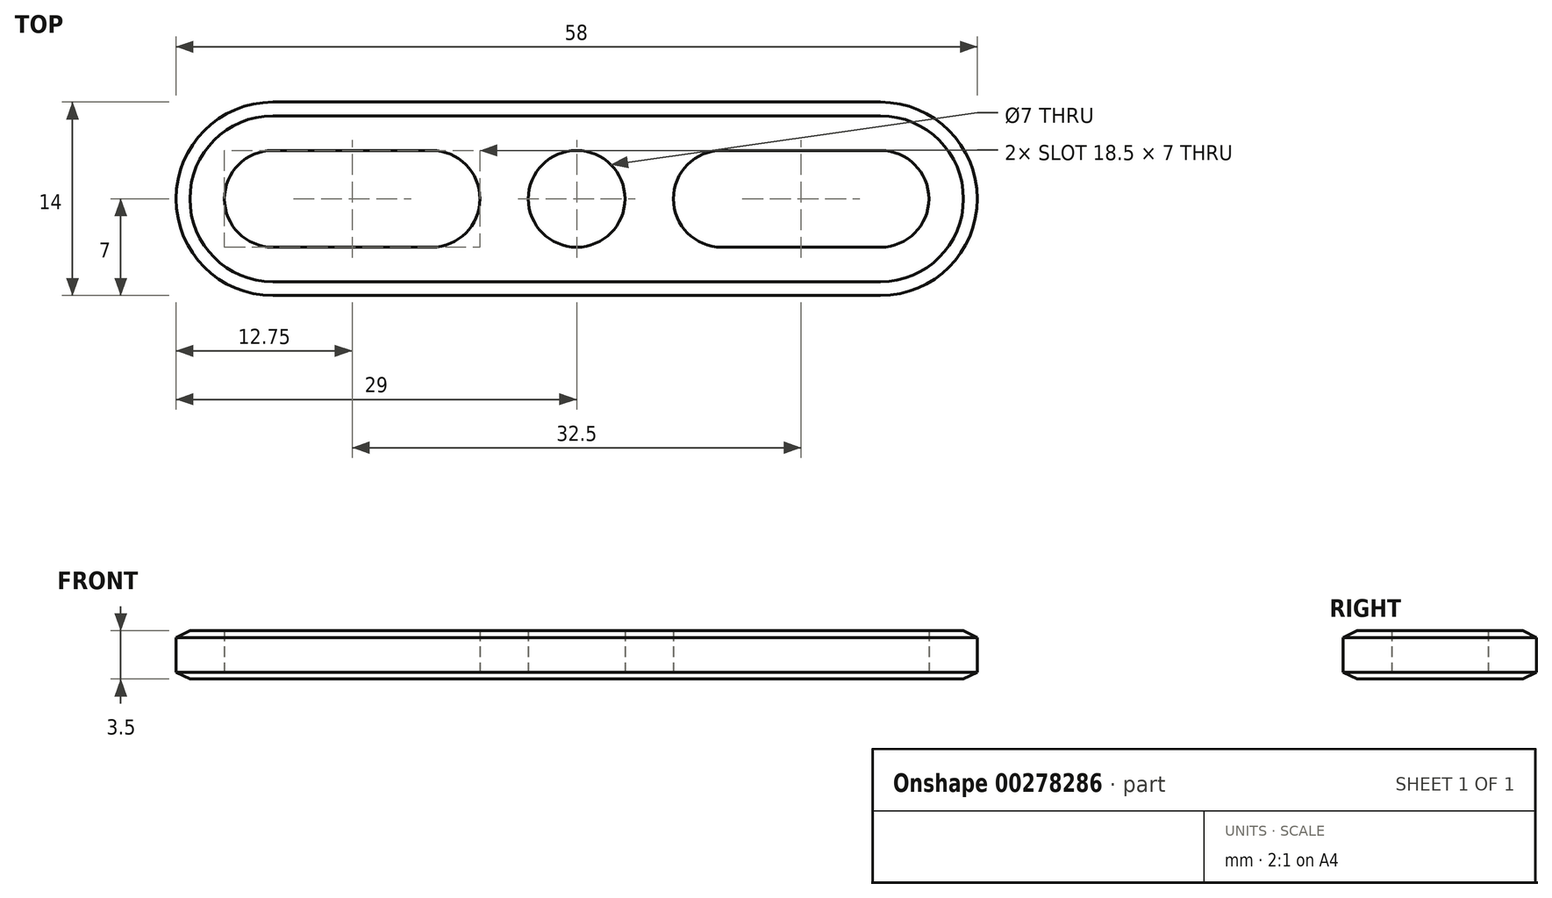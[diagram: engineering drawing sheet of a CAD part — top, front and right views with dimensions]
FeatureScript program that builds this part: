
annotation { "Feature Type Name" : "Feature", "Feature Type Description" : "" }
export const myFeature = defineFeature(function(context is Context, id is Id, definition is map)
    precondition{}
    {
        {
            var Q0;
            Q0=qCreatedBy(makeId("Top.planeOp"),FACE);
            var sketch = newSketch(context, id + "F0", { "sketchPlane" : qUnion([Q0])});
            skLineSegment(sketch, "E0", {"start": v(0, 0) * mm, "end": v(44, 0) * mm});
            skArc(sketch, "E1", {"start": v(0, 14) * mm, "mid": v(-7, 7) * mm, "end": v(0, 0) * mm});
            skLineSegment(sketch, "E2", {"start": v(0, 14) * mm, "end": v(44, 14) * mm});
            skArc(sketch, "E3", {"start": v(44, 0) * mm, "mid": v(51, 7) * mm, "end": v(44, 14) * mm});
            skCircle(sketch, "E4", {"center": v(22, 7) * mm, "radius": 3.5 * mm});
            skLineSegment(sketch, "E5", {"start": v(0, 10.5) * mm, "end": v(11.5, 10.5) * mm});
            skLineSegment(sketch, "E6", {"start": v(0, 3.5) * mm, "end": v(11.5, 3.5) * mm});
            skArc(sketch, "E7", {"start": v(0, 10.5) * mm, "mid": v(-3.5, 7) * mm, "end": v(0, 3.5) * mm});
            skArc(sketch, "E8", {"start": v(11.5, 3.5) * mm, "mid": v(15, 7) * mm, "end": v(11.5, 10.5) * mm});
            skLineSegment(sketch, "E9", {"start": v(32.5, 10.5) * mm, "end": v(44, 10.5) * mm});
            skLineSegment(sketch, "E10", {"start": v(32.5, 3.5) * mm, "end": v(44, 3.5) * mm});
            skArc(sketch, "E11", {"start": v(32.5, 10.5) * mm, "mid": v(29, 7) * mm, "end": v(32.5, 3.5) * mm});
            skArc(sketch, "E12", {"start": v(44, 3.5) * mm, "mid": v(47.5, 7) * mm, "end": v(44, 10.5) * mm});
            skSolve(sketch);
        }
        {
            var Q0;
            Q0 = qSketchRegion(id + "F0", true);
            extrude(context, id + "F1", {"entities" : qUnion([Q0]), "depth" : 3.5 * mm, "offsetDistance" : 25 * mm});
        }
        {
            var Q0;
            Q0=makeQuery(id+"F1.opExtrude","CAP_EDGE",EDGE,{"disambiguationData":[OSD([sQuery(id+"F0.wireOp",EDGE,"E0")])],"isStart":false});
            var Q1;
            Q1=makeQuery(id+"F1.opExtrude","CAP_EDGE",EDGE,{"disambiguationData":[OSD([sQuery(id+"F0.wireOp",EDGE,"E0")])],"isStart":true});
            chamfer(context, id + "F2", {"entities" : qUnion([Q0, Q1]), "chamferType" : ChamferType.TWO_OFFSETS, "width1" : 0.5 * mm, "oppositeDirection" : false, "width2" : 1 * mm, "tangentPropagation" : true});
        }
    });
